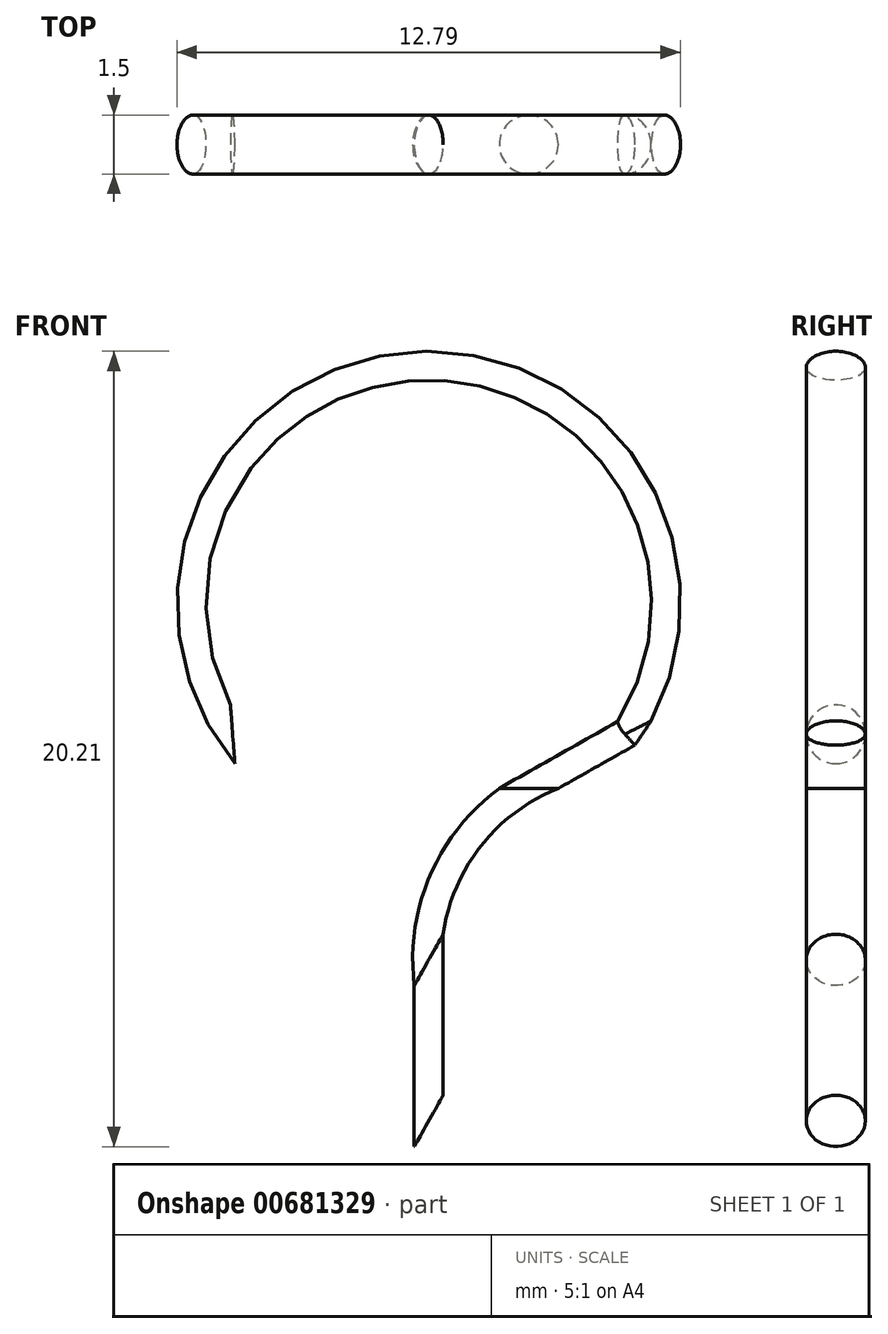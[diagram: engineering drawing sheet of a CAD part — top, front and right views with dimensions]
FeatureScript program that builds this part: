
annotation { "Feature Type Name" : "Feature", "Feature Type Description" : "" }
export const myFeature = defineFeature(function(context is Context, id is Id, definition is map)
    precondition{}
    {
        {
            var Q0;
            Q0=qCreatedBy(makeId("Front.planeOp"),FACE);
            var sketch = newSketch(context, id + "F0", { "sketchPlane" : qUnion([Q0])});
            skArc(sketch, "E0", {"start": v(0, 0) * mm, "mid": v(-4.98, 9.33) * mm, "end": v(-9.96, 0) * mm});
            skPoint(sketch, "E1", {"position": v(-4.98, 9.33) * mm});
            skLineSegment(sketch, "E2", {"start": v(0, 0) * mm, "end": v(-2.44, -1.38) * mm});
            skLineSegment(sketch, "E3", {"start": v(-4.98, -5.73) * mm, "end": v(-4.98, -9.82) * mm});
            skPoint(sketch, "E4.visualSharp", {"position": v(-4.98, -2.81) * mm});
            skArc(sketch, "E4.filletArc", {"start": v(-2.44, -1.38) * mm, "mid": v(-4.3, -3.21) * mm, "end": v(-4.98, -5.73) * mm});
            skSolve(sketch);
        }
        {
            var Q0;
            Q0=qCreatedBy(makeId("Top.planeOp"),FACE);
            var sketch = newSketch(context, id + "F1", { "sketchPlane" : qUnion([Q0])});
            skCircle(sketch, "E5", {"center": v(0, 0) * mm, "radius": 0.75 * mm});
            skSolve(sketch);
        }
        {
            var Q0;
            Q0=makeQuery(id+"F1.imprint","IMPRINT",FACE,{"disambiguationData":[TD([[makeQuery(id+"F1.imprint","IMPRINT",EDGE,{"derivedFrom":sQuery(id+"F1.wireOp",EDGE,"E5")}),1.0]])]});
            var Q1;
            Q1=sQuery(id+"F0.wireOp",EDGE,"E4.filletArc");
            var Q2;
            Q2=sQuery(id+"F0.wireOp",EDGE,"E2");
            var Q3;
            Q3=sQuery(id+"F0.wireOp",EDGE,"E0");
            var Q4;
            Q4=sQuery(id+"F0.wireOp",EDGE,"E3");
            sweep(context, id + "F2", {"profiles" : qUnion([Q0]), "path" : qUnion([Q1, Q2, Q3, Q4])});
        }
    });
